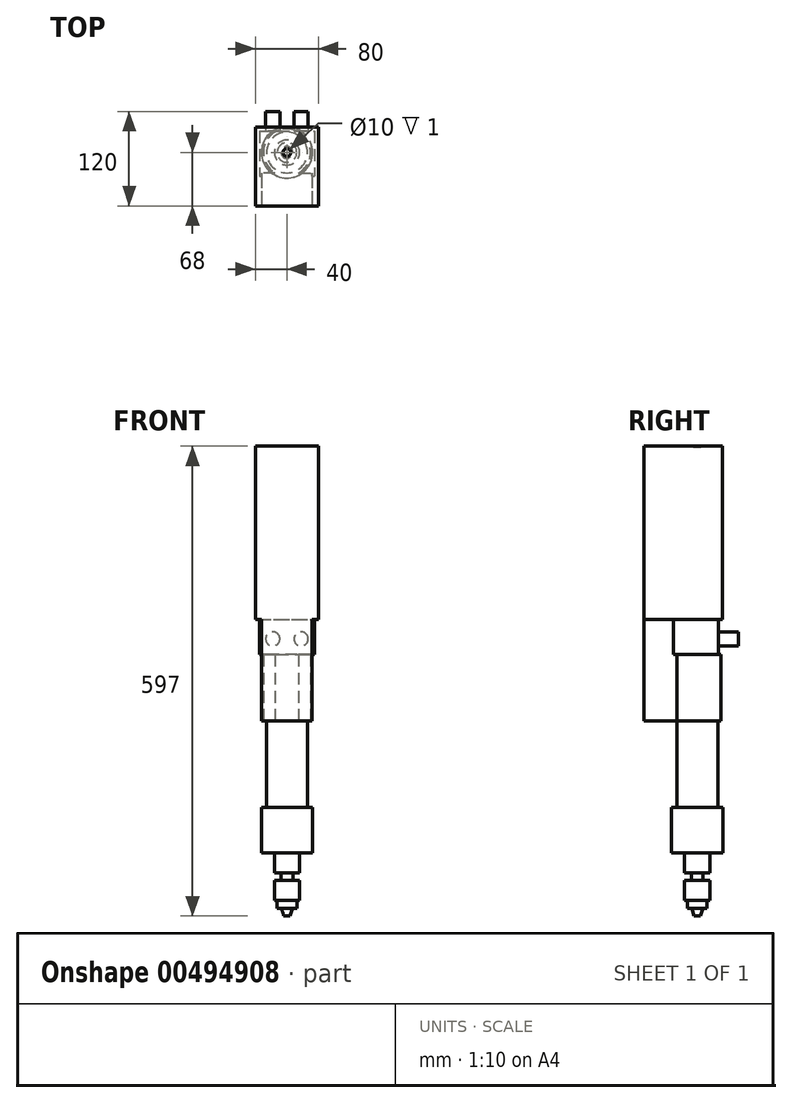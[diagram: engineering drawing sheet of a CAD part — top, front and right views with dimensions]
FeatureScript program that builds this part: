
annotation { "Feature Type Name" : "Feature", "Feature Type Description" : "" }
export const myFeature = defineFeature(function(context is Context, id is Id, definition is map)
    precondition{}
    {
        {
            var Q0;
            Q0=qCreatedBy(makeId("Top.planeOp"),FACE);
            var sketch = newSketch(context, id + "F0", { "sketchPlane" : qUnion([Q0])});
            skCircle(sketch, "E0", {"center": v(0, 0) * mm, "radius": 32.5 * mm});
            skSolve(sketch);
        }
        {
            var Q0;
            Q0=qSketchRegion(id+"F0",true);
            extrude(context, id + "F1", {"entities" : qUnion([Q0]), "oppositeDirection" : true, "depth" : 58 * mm});
        }
        {
            var Q0;
            Q0=makeQuery(id+"F1.opExtrude","CAP_FACE",FACE,{"disambiguationData":[OSD([sQuery(id+"F0.wireOp",EDGE,"E0")])],"isStart":false});
            var sketch = newSketch(context, id + "F2", { "sketchPlane" : qUnion([Q0])});
            skCircle(sketch, "E1", {"center": v(0, 0) * mm, "radius": 16 * mm});
            skSolve(sketch);
        }
        {
            var Q0;
            Q0=qSketchRegion(id+"F2",true);
            extrude(context, id + "F3", {"entities" : qUnion([Q0]), "operationType" : NewBodyOperationType.ADD, "depth" : 25 * mm});
        }
        {
            var Q0;
            Q0=qCreatedBy(makeId("Top.planeOp"),FACE);
            var sketch = newSketch(context, id + "F4", { "sketchPlane" : qUnion([Q0])});
            skCircle(sketch, "E2", {"center": v(0, 0) * mm, "radius": 26 * mm});
            skSolve(sketch);
        }
        {
            var Q0;
            Q0=qSketchRegion(id+"F4",true);
            extrude(context, id + "F5", {"entities" : qUnion([Q0]), "operationType" : NewBodyOperationType.ADD, "depth" : 110 * mm});
        }
        {
            var Q0;
            Q0=makeQuery(id+"F5.opExtrude","CAP_FACE",FACE,{"disambiguationData":[OSD([sQuery(id+"F4.wireOp",EDGE,"E2")])],"isStart":false});
            var sketch = newSketch(context, id + "F6", { "sketchPlane" : qUnion([Q0])});
            skCircle(sketch, "E3", {"center": v(0, 0) * mm, "radius": 30 * mm});
            skSolve(sketch);
        }
        {
            var Q0;
            Q0=qSketchRegion(id+"F6",true);
            extrude(context, id + "F7", {"entities" : qUnion([Q0]), "operationType" : NewBodyOperationType.ADD, "depth" : (252 - 58 - 110) * mm});
        }
        {
            var Q0;
            Q0=makeQuery(id+"F7.opExtrude","CAP_FACE",FACE,{"disambiguationData":[OSD([sQuery(id+"F6.wireOp",EDGE,"E3")])],"isStart":false});
            var sketch = newSketch(context, id + "F8", { "sketchPlane" : qUnion([Q0])});
            skLineSegment(sketch, "E4.bottom", {"start": v(-35, 27) * mm, "end": v(35, 27) * mm});
            skLineSegment(sketch, "E4.top", {"start": v(-35, -30) * mm, "end": v(35, -30) * mm});
            skLineSegment(sketch, "E4.left", {"start": v(-35, 27) * mm, "end": v(-35, -30) * mm});
            skLineSegment(sketch, "E4.right", {"start": v(35, 27) * mm, "end": v(35, -30) * mm});
            skSolve(sketch);
        }
        {
            var Q0;
            Q0=qSketchRegion(id+"F8",true);
            extrude(context, id + "F9", {"entities" : qUnion([Q0]), "operationType" : NewBodyOperationType.ADD, "depth" : 85 * mm});
        }
        {
            var Q0;
            Q0=makeQuery(id+"F7.opExtrude","CAP_FACE",FACE,{"disambiguationData":[OSD([sQuery(id+"F6.wireOp",EDGE,"E3")])],"isStart":true});
            var sketch = newSketch(context, id + "F10", { "sketchPlane" : qUnion([Q0])});
            skLineSegment(sketch, "E5.bottom", {"start": v(-32, 26) * mm, "end": v(32, 26) * mm});
            skLineSegment(sketch, "E5.top", {"start": v(-32, 68) * mm, "end": v(32, 68) * mm});
            skLineSegment(sketch, "E5.left", {"start": v(-32, 26) * mm, "end": v(-32, 68) * mm});
            skLineSegment(sketch, "E5.right", {"start": v(32, 26) * mm, "end": v(32, 68) * mm});
            skSolve(sketch);
        }
        {
            var Q0;
            Q0=qSketchRegion(id+"F10",true);
            var Q1;
            Q1=makeQuery(id+"F9.opExtrude","CAP_FACE",FACE,{"disambiguationData":[OSD([sQuery(id+"F8.wireOp",EDGE,"E4.bottom"),sQuery(id+"F8.wireOp",EDGE,"E4.top"),sQuery(id+"F8.wireOp",EDGE,"E4.left"),sQuery(id+"F8.wireOp",EDGE,"E4.right")])],"isStart":false});
            extrude(context, id + "F11", {"entities" : qUnion([Q0]), "operationType" : NewBodyOperationType.ADD, "endBound" : BoundingType.UP_TO_SURFACE, "oppositeDirection" : true, "endBoundEntityFace" : qUnion([Q1]), "depth" : 25 * mm});
        }
        {
            var Q0;
            {var subQ0=sQuery(id+"F8.wireOp",EDGE,"E4.right");var subQ1=sQuery(id+"F8.wireOp",EDGE,"E4.left");var subQ2=sQuery(id+"F8.wireOp",EDGE,"E4.top");var subQ3=sQuery(id+"F8.wireOp",EDGE,"E4.bottom");Q0=makeQuery(id+"F11.boolean.opBoolean","MERGE",FACE,{"derivedFrom":[makeQuery(id+"F9.opExtrude","CAP_FACE",FACE,{"disambiguationData":[OSD([subQ3,subQ2,subQ1,subQ0])],"isStart":false}),makeQuery(id+"F11.opExtrude","CAP_FACE",FACE,{"disambiguationData":[OSD([subQ3,subQ2,subQ1,subQ0])],"isStart":false})]});}
            var sketch = newSketch(context, id + "F12", { "sketchPlane" : qUnion([Q0])});
            skLineSegment(sketch, "E6.bottom", {"start": v(-40, 32) * mm, "end": v(40, 32) * mm});
            skLineSegment(sketch, "E6.top", {"start": v(-40, -68) * mm, "end": v(40, -68) * mm});
            skLineSegment(sketch, "E6.left", {"start": v(-40, 32) * mm, "end": v(-40, -68) * mm});
            skLineSegment(sketch, "E6.right", {"start": v(40, 32) * mm, "end": v(40, -68) * mm});
            skSolve(sketch);
        }
        {
            var Q0;
            Q0=qSketchRegion(id+"F12",true);
            extrude(context, id + "F13", {"entities" : qUnion([Q0]), "operationType" : NewBodyOperationType.ADD, "depth" : 180 * mm, "hasSecondDirection" : true, "secondDirectionOppositeDirection" : true, "secondDirectionDepth" : 40 * mm});
        }
        {
            var Q0;
            Q0=makeQuery(id+"F9.opExtrude","SWEPT_FACE",FACE,{"disambiguationData":[OSD([sQuery(id+"F8.wireOp",EDGE,"E4.bottom")])]});
            var sketch = newSketch(context, id + "F14", { "sketchPlane" : qUnion([Q0])});
            skCircle(sketch, "E7", {"center": v(18, 214) * mm, "radius": 9 * mm});
            skCircle(sketch, "E8", {"center": v(-18, 214) * mm, "radius": 9 * mm});
            skSolve(sketch);
        }
        {
            var Q0;
            Q0=qSketchRegion(id+"F14",true);
            extrude(context, id + "F15", {"entities" : qUnion([Q0]), "operationType" : NewBodyOperationType.ADD, "depth" : 25 * mm});
        }
        {
            var Q0;
            Q0=makeQuery(id+"F3.opExtrude","CAP_FACE",FACE,{"disambiguationData":[OSD([sQuery(id+"F2.wireOp",EDGE,"E1")])],"isStart":false});
            var sketch = newSketch(context, id + "F16", { "sketchPlane" : qUnion([Q0])});
            skCircle(sketch, "E9", {"center": v(0, 0) * mm, "radius": 7.5 * mm});
            skSolve(sketch);
        }
        {
            var Q0;
            Q0=qSketchRegion(id+"F16",true);
            extrude(context, id + "F17", {"entities" : qUnion([Q0]), "operationType" : NewBodyOperationType.ADD, "depth" : 10 * mm});
        }
        {
            var Q0;
            Q0=makeQuery(id+"F17.opExtrude","CAP_FACE",FACE,{"disambiguationData":[OSD([sQuery(id+"F16.wireOp",EDGE,"E9")])],"isStart":false});
            var sketch = newSketch(context, id + "F18", { "sketchPlane" : qUnion([Q0])});
            skCircle(sketch, "E10", {"center": v(0, 0) * mm, "radius": 16 * mm});
            skSolve(sketch);
        }
        {
            var Q0;
            Q0=qSketchRegion(id+"F18",true);
            extrude(context, id + "F19", {"entities" : qUnion([Q0]), "operationType" : NewBodyOperationType.ADD, "depth" : 25 * mm});
        }
        {
            var Q0;
            Q0=makeQuery(id+"F19.opExtrude","CAP_FACE",FACE,{"disambiguationData":[OSD([sQuery(id+"F18.wireOp",EDGE,"E10")])],"isStart":false});
            var sketch = newSketch(context, id + "F20", { "sketchPlane" : qUnion([Q0])});
            skCircle(sketch, "E11", {"center": v(0, 0) * mm, "radius": 12.5 * mm});
            skSolve(sketch);
        }
        {
            var Q0;
            Q0=qSketchRegion(id+"F20",true);
            extrude(context, id + "F21", {"entities" : qUnion([Q0]), "operationType" : NewBodyOperationType.ADD, "depth" : 10 * mm});
        }
        {
            var Q0;
            Q0=qCreatedBy(makeId("Front.planeOp"),FACE);
            var sketch = newSketch(context, id + "F22", { "sketchPlane" : qUnion([Q0])});
            skLineSegment(sketch, "E12", {"start": v(0, -128) * mm, "end": v(0, -138) * mm});
            skLineSegment(sketch, "E13", {"start": v(0, -138) * mm, "end": v(-4, -138) * mm});
            skLineSegment(sketch, "E14", {"start": v(-4, -138) * mm, "end": v(-7, -128) * mm});
            skLineSegment(sketch, "E15", {"start": v(-7, -128) * mm, "end": v(0, -128) * mm});
            skSolve(sketch);
        }
        {
            var Q0;
            Q0=qSketchRegion(id+"F22",true);
            var Q1;
            Q1=makeQuery(id+"F3.opExtrude","SWEPT_FACE",FACE,{"disambiguationData":[OSD([sQuery(id+"F2.wireOp",EDGE,"E1")])]});
            revolve(context, id + "F23", {"operationType" : NewBodyOperationType.ADD, "entities" : qUnion([Q0]), "axis" : qUnion([Q1]), "revolveType" : RevolveType.FULL});
        }
        {
            var Q0;
            Q0=makeQuery(id+"F13.opExtrude","CAP_FACE",FACE,{"disambiguationData":[OSD([sQuery(id+"F12.wireOp",EDGE,"E6.bottom"),sQuery(id+"F12.wireOp",EDGE,"E6.top"),sQuery(id+"F12.wireOp",EDGE,"E6.left"),sQuery(id+"F12.wireOp",EDGE,"E6.right")])],"isStart":false});
            var sketch = newSketch(context, id + "F24", { "sketchPlane" : qUnion([Q0])});
            skCircle(sketch, "E16", {"center": v(0, 0) * mm, "radius": 5 * mm});
            skSolve(sketch);
        }
        {
            var Q0;
            Q0=qSketchRegion(id+"F24",true);
            extrude(context, id + "F25", {"entities" : qUnion([Q0]), "operationType" : NewBodyOperationType.REMOVE, "oppositeDirection" : true, "depth" : 1 * mm});
        }
    });
